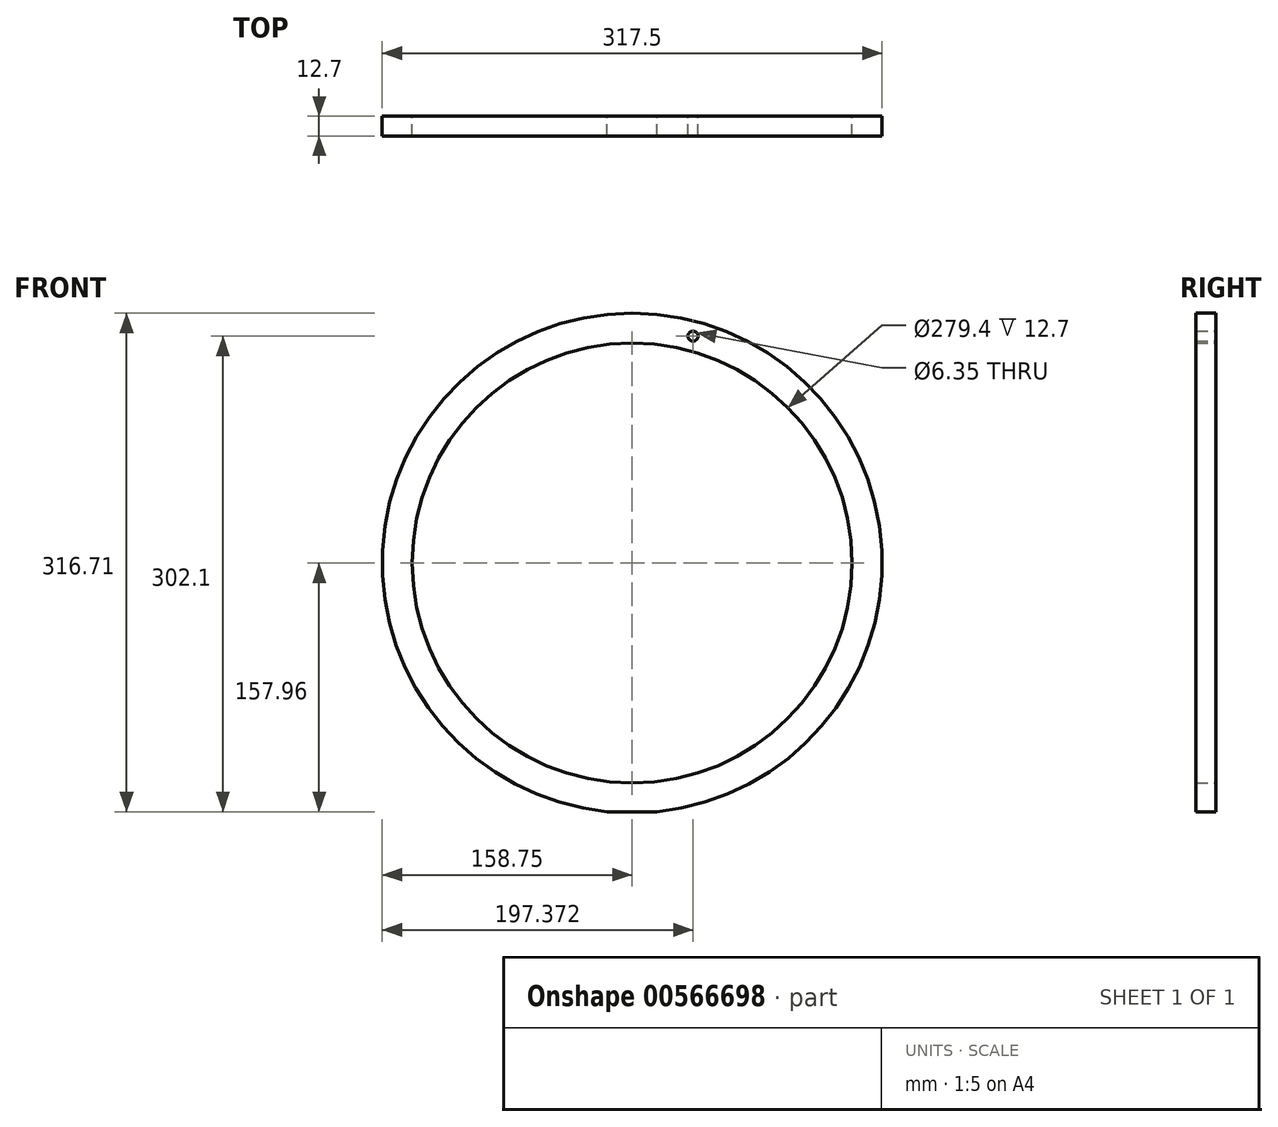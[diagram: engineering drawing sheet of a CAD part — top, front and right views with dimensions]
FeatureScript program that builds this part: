
annotation { "Feature Type Name" : "Feature", "Feature Type Description" : "" }
export const myFeature = defineFeature(function(context is Context, id is Id, definition is map)
    precondition{}
    {
        {
            var Q0;
            Q0=qCreatedBy(makeId("Front.planeOp"),FACE);
            var sketch = newSketch(context, id + "F0", { "sketchPlane" : qUnion([Q0])});
            skCircle(sketch, "E0", {"center": v(0, 0) * mm, "radius": 139.7 * mm});
            skLineSegment(sketch, "E1", {"start": v(-15.86, -157.96) * mm, "end": v(15.86, -157.96) * mm});
            skArc(sketch, "E2", {"start": v(-15.86, -157.96) * mm, "mid": v(0, -158.75) * mm, "end": v(15.86, -157.96) * mm, "construction": true});
            skArc(sketch, "E3", {"start": v(15.86, -157.96) * mm, "mid": v(0, 158.75) * mm, "end": v(-15.86, -157.96) * mm});
            skSolve(sketch);
        }
        {
            var Q0;
            Q0=makeQuery(id+"F0.imprint","IMPRINT",FACE,{"disambiguationData":[TD([[makeQuery(id+"F0.imprint","IMPRINT",EDGE,{"derivedFrom":sQuery(id+"F0.wireOp",EDGE,"E0")}),-1.0]])]});
            extrude(context, id + "F1", {"entities" : qUnion([Q0]), "depth" : 12.7 * mm, "offsetDistance" : 25.4 * mm});
        }
        {
            var Q0;
            Q0=makeQuery(id+"F0.imprint","IMPRINT",FACE,{"disambiguationData":[TD([[makeQuery(id+"F0.imprint","IMPRINT",EDGE,{"derivedFrom":sQuery(id+"F0.wireOp",EDGE,"E0")}),1.0]])]});
            var sketch = newSketch(context, id + "F2", { "sketchPlane" : qUnion([Q0])});
            skArc(sketch, "E4.0", {"start": v(15.86, -157.96) * mm, "mid": v(0, 158.75) * mm, "end": v(-15.86, -157.96) * mm, "construction": true});
            skCircle(sketch, "E5.0", {"center": v(0, 0) * mm, "radius": 139.7 * mm, "construction": true});
            skLineSegment(sketch, "E6.0", {"start": v(-15.86, -157.96) * mm, "end": v(15.86, -157.96) * mm});
            skArc(sketch, "E7.0", {"start": v(-15.86, -157.96) * mm, "mid": v(0, -158.75) * mm, "end": v(15.86, -157.96) * mm});
            skCircle(sketch, "E8", {"center": v(0, 149.22) * mm, "radius": 1.59 * mm});
            skLineSegment(sketch, "E9", {"start": v(0, 149.22) * mm, "end": v(29, 149.22) * mm, "construction": true});
            skLineSegment(sketch, "E10", {"start": v(0, 149.22) * mm, "end": v(0, 0) * mm, "construction": true});
            skCircle(sketch, "E11.1.0.0", {"center": v(2.75, 147.64) * mm, "radius": 1.59 * mm});
            skCircle(sketch, "E11.2.0.0", {"center": v(5.5, 146.05) * mm, "radius": 1.59 * mm});
            skLineSegment(sketch, "E11.direction1", {"start": v(0, 149.22) * mm, "end": v(2.75, 147.64) * mm, "construction": true});
            skCircle(sketch, "E12.cCircle", {"center": v(0, 149.22) * mm, "radius": 6.35 * mm, "construction": true});
            skLineSegment(sketch, "E12.0", {"start": v(5.5, 146.05) * mm, "end": v(0, 142.87) * mm});
            skLineSegment(sketch, "E12.1", {"start": v(0, 142.88) * mm, "end": v(-5.5, 146.05) * mm});
            skLineSegment(sketch, "E12.2", {"start": v(-5.5, 146.05) * mm, "end": v(-5.5, 152.4) * mm});
            skLineSegment(sketch, "E12.3", {"start": v(-5.5, 152.4) * mm, "end": v(0, 155.57) * mm});
            skLineSegment(sketch, "E12.4", {"start": v(0, 155.57) * mm, "end": v(5.5, 152.4) * mm});
            skLineSegment(sketch, "E12.5", {"start": v(5.5, 152.4) * mm, "end": v(5.5, 146.05) * mm});
            skLineSegment(sketch, "E13", {"start": v(0, 149.22) * mm, "end": v(-5.5, 146.05) * mm});
            skLineSegment(sketch, "E14.bottom", {"start": v(-5.5, 152.4) * mm, "end": v(5.5, 152.4) * mm});
            skLineSegment(sketch, "E14.top", {"start": v(-5.5, 146.05) * mm, "end": v(5.5, 146.05) * mm});
            skLineSegment(sketch, "E14.left", {"start": v(-5.5, 152.4) * mm, "end": v(-5.5, 146.05) * mm});
            skCircle(sketch, "E15.1.0", {"center": v(2.75, 150.81) * mm, "radius": 1.59 * mm});
            skCircle(sketch, "E15.1.1", {"center": v(5.5, 152.4) * mm, "radius": 1.59 * mm});
            skCircle(sketch, "E15.2.0", {"center": v(0, 152.4) * mm, "radius": 1.59 * mm});
            skCircle(sketch, "E15.2.1", {"center": v(0, 155.57) * mm, "radius": 1.59 * mm});
            skCircle(sketch, "E15.3.0", {"center": v(-2.75, 150.81) * mm, "radius": 1.59 * mm});
            skCircle(sketch, "E15.3.1", {"center": v(-5.5, 152.4) * mm, "radius": 1.59 * mm});
            skCircle(sketch, "E15.4.0", {"center": v(-2.75, 147.64) * mm, "radius": 1.59 * mm});
            skCircle(sketch, "E15.4.1", {"center": v(-5.5, 146.05) * mm, "radius": 1.59 * mm});
            skCircle(sketch, "E15.5.0", {"center": v(0, 146.05) * mm, "radius": 1.59 * mm});
            skCircle(sketch, "E15.5.1", {"center": v(0, 142.88) * mm, "radius": 1.59 * mm});
            skLineSegment(sketch, "E16.1.0", {"start": v(0, 149.22) * mm, "end": v(0, 142.88) * mm});
            skLineSegment(sketch, "E16.1.1", {"start": v(0, 149.22) * mm, "end": v(2.75, 150.81) * mm, "construction": true});
            skLineSegment(sketch, "E16.2.0", {"start": v(0, 149.22) * mm, "end": v(5.5, 146.05) * mm});
            skLineSegment(sketch, "E16.2.1", {"start": v(0, 149.22) * mm, "end": v(0, 152.4) * mm, "construction": true});
            skLineSegment(sketch, "E16.3.0", {"start": v(0, 149.22) * mm, "end": v(5.5, 152.4) * mm});
            skLineSegment(sketch, "E16.3.1", {"start": v(0, 149.22) * mm, "end": v(-2.75, 150.81) * mm, "construction": true});
            skLineSegment(sketch, "E16.4.0", {"start": v(0, 149.22) * mm, "end": v(0, 155.57) * mm});
            skLineSegment(sketch, "E16.4.1", {"start": v(0, 149.22) * mm, "end": v(-2.75, 147.64) * mm, "construction": true});
            skLineSegment(sketch, "E16.5.0", {"start": v(0, 149.22) * mm, "end": v(-5.5, 152.4) * mm});
            skLineSegment(sketch, "E16.5.1", {"start": v(0, 149.22) * mm, "end": v(0, 146.05) * mm, "construction": true});
            skLineSegment(sketch, "E17", {"start": v(-5.5, 152.4) * mm, "end": v(0, 142.88) * mm});
            skLineSegment(sketch, "E18", {"start": v(0, 142.87) * mm, "end": v(5.5, 152.4) * mm});
            skLineSegment(sketch, "E19", {"start": v(-2.75, 150.81) * mm, "end": v(0, 146.05) * mm});
            skLineSegment(sketch, "E20", {"start": v(0, 146.05) * mm, "end": v(2.75, 150.81) * mm});
            skLineSegment(sketch, "E21", {"start": v(2.75, 150.81) * mm, "end": v(-2.75, 150.81) * mm});
            skLineSegment(sketch, "E22", {"start": v(-2.75, 150.81) * mm, "end": v(0, 152.4) * mm});
            skLineSegment(sketch, "E23", {"start": v(0, 152.4) * mm, "end": v(2.75, 150.81) * mm});
            skLineSegment(sketch, "E24", {"start": v(2.75, 150.81) * mm, "end": v(2.75, 147.64) * mm});
            skLineSegment(sketch, "E25", {"start": v(2.75, 147.64) * mm, "end": v(0, 146.05) * mm});
            skLineSegment(sketch, "E26", {"start": v(0, 146.05) * mm, "end": v(-2.75, 147.64) * mm});
            skLineSegment(sketch, "E27", {"start": v(-2.75, 147.64) * mm, "end": v(-2.75, 150.81) * mm});
            skLineSegment(sketch, "E28", {"start": v(0, 152.4) * mm, "end": v(-2.75, 147.64) * mm});
            skLineSegment(sketch, "E29", {"start": v(0, 152.4) * mm, "end": v(2.75, 147.64) * mm});
            skLineSegment(sketch, "E30", {"start": v(2.75, 147.64) * mm, "end": v(-2.75, 147.64) * mm});
            skLineSegment(sketch, "E31", {"start": v(0, 142.88) * mm, "end": v(-2.75, 150.81) * mm});
            skLineSegment(sketch, "E32", {"start": v(0, 142.88) * mm, "end": v(2.75, 150.81) * mm});
            skLineSegment(sketch, "E33", {"start": v(5.5, 146.05) * mm, "end": v(-2.75, 147.64) * mm});
            skLineSegment(sketch, "E34", {"start": v(5.5, 146.05) * mm, "end": v(0, 152.4) * mm});
            skLineSegment(sketch, "E35", {"start": v(5.5, 152.4) * mm, "end": v(0, 146.05) * mm});
            skLineSegment(sketch, "E36", {"start": v(5.5, 152.4) * mm, "end": v(-2.75, 150.81) * mm});
            skLineSegment(sketch, "E37", {"start": v(0, 155.57) * mm, "end": v(2.75, 147.64) * mm});
            skLineSegment(sketch, "E38", {"start": v(0, 155.57) * mm, "end": v(-2.75, 147.64) * mm});
            skLineSegment(sketch, "E39", {"start": v(-5.5, 152.4) * mm, "end": v(2.75, 150.81) * mm});
            skLineSegment(sketch, "E40", {"start": v(-5.5, 152.4) * mm, "end": v(0, 146.05) * mm});
            skLineSegment(sketch, "E41", {"start": v(-5.5, 146.05) * mm, "end": v(2.75, 147.64) * mm});
            skLineSegment(sketch, "E42", {"start": v(-5.5, 146.05) * mm, "end": v(0, 152.4) * mm});
            skLineSegment(sketch, "E43", {"start": v(0, 155.57) * mm, "end": v(-5.5, 146.05) * mm});
            skLineSegment(sketch, "E44", {"start": v(0, 155.57) * mm, "end": v(5.5, 146.05) * mm});
            skCircle(sketch, "E45.1.0", {"center": v(-129.23, 74.61) * mm, "radius": 6.35 * mm, "construction": true});
            skLineSegment(sketch, "E45.1.1", {"start": v(-129.23, 80.96) * mm, "end": v(-131.98, 73.03) * mm});
            skLineSegment(sketch, "E45.1.2", {"start": v(-134.73, 71.44) * mm, "end": v(-123.73, 71.44) * mm});
            skCircle(sketch, "E45.1.3", {"center": v(-131.98, 73.03) * mm, "radius": 1.59 * mm});
            skLineSegment(sketch, "E45.1.4", {"start": v(-129.23, 74.61) * mm, "end": v(-126.48, 76.2) * mm, "construction": true});
            skLineSegment(sketch, "E45.1.5", {"start": v(-123.73, 77.79) * mm, "end": v(-129.23, 71.44) * mm});
            skLineSegment(sketch, "E45.1.6", {"start": v(-129.23, 80.96) * mm, "end": v(-126.48, 73.03) * mm});
            skCircle(sketch, "E45.1.7", {"center": v(-129.23, 77.79) * mm, "radius": 1.59 * mm});
            skCircle(sketch, "E45.1.8", {"center": v(-123.73, 77.79) * mm, "radius": 1.59 * mm});
            skLineSegment(sketch, "E45.1.9", {"start": v(-131.98, 76.2) * mm, "end": v(-126.48, 76.2) * mm});
            skLineSegment(sketch, "E45.1.10", {"start": v(-126.48, 73.03) * mm, "end": v(-129.23, 77.79) * mm});
            skCircle(sketch, "E45.1.11", {"center": v(-134.73, 71.44) * mm, "radius": 1.59 * mm});
            skLineSegment(sketch, "E45.1.12", {"start": v(-123.73, 77.79) * mm, "end": v(-131.98, 76.2) * mm});
            skLineSegment(sketch, "E45.1.13", {"start": v(-123.73, 71.44) * mm, "end": v(-129.23, 80.96) * mm});
            skCircle(sketch, "E45.1.14", {"center": v(-126.48, 76.2) * mm, "radius": 1.59 * mm});
            skLineSegment(sketch, "E45.1.15", {"start": v(-129.23, 74.61) * mm, "end": v(-134.73, 77.79) * mm});
            skCircle(sketch, "E45.1.16", {"center": v(-129.23, 68.26) * mm, "radius": 1.59 * mm});
            skLineSegment(sketch, "E45.1.17", {"start": v(-123.73, 71.44) * mm, "end": v(-129.23, 68.26) * mm});
            skCircle(sketch, "E45.1.18", {"center": v(-129.23, 74.61) * mm, "radius": 1.59 * mm});
            skCircle(sketch, "E45.1.19", {"center": v(-134.73, 77.79) * mm, "radius": 1.59 * mm});
            skCircle(sketch, "E45.1.20", {"center": v(-129.23, 71.44) * mm, "radius": 1.59 * mm});
            skLineSegment(sketch, "E45.1.21", {"start": v(-123.73, 77.79) * mm, "end": v(-123.73, 71.44) * mm});
            skLineSegment(sketch, "E45.1.22", {"start": v(-129.23, 74.61) * mm, "end": v(-126.48, 73.03) * mm, "construction": true});
            skLineSegment(sketch, "E45.1.23", {"start": v(-123.73, 71.44) * mm, "end": v(-129.23, 77.79) * mm});
            skLineSegment(sketch, "E45.1.24", {"start": v(-134.73, 77.79) * mm, "end": v(-129.23, 80.96) * mm});
            skLineSegment(sketch, "E45.1.25", {"start": v(-134.73, 71.44) * mm, "end": v(-134.73, 77.79) * mm});
            skLineSegment(sketch, "E45.1.26", {"start": v(-129.23, 68.26) * mm, "end": v(-134.73, 71.44) * mm});
            skLineSegment(sketch, "E45.1.27", {"start": v(-131.98, 76.2) * mm, "end": v(-129.23, 71.44) * mm});
            skLineSegment(sketch, "E45.1.28", {"start": v(-134.73, 77.79) * mm, "end": v(-123.73, 77.79) * mm});
            skLineSegment(sketch, "E45.1.29", {"start": v(-131.98, 73.03) * mm, "end": v(-126.48, 73.03) * mm});
            skLineSegment(sketch, "E45.1.30", {"start": v(-129.23, 68.26) * mm, "end": v(-126.48, 76.2) * mm});
            skLineSegment(sketch, "E45.1.31", {"start": v(-126.48, 76.2) * mm, "end": v(-126.48, 73.03) * mm});
            skLineSegment(sketch, "E45.1.32", {"start": v(-129.23, 74.61) * mm, "end": v(-131.98, 73.03) * mm, "construction": true});
            skLineSegment(sketch, "E45.1.33", {"start": v(-129.23, 74.61) * mm, "end": v(-134.73, 71.44) * mm});
            skCircle(sketch, "E45.1.34", {"center": v(-131.98, 76.2) * mm, "radius": 1.59 * mm});
            skLineSegment(sketch, "E45.1.35", {"start": v(-123.73, 71.44) * mm, "end": v(-131.98, 73.03) * mm});
            skCircle(sketch, "E45.1.36", {"center": v(-126.48, 73.03) * mm, "radius": 1.59 * mm});
            skLineSegment(sketch, "E45.1.37", {"start": v(-134.73, 77.79) * mm, "end": v(-126.48, 76.2) * mm});
            skLineSegment(sketch, "E45.1.38", {"start": v(-129.23, 77.79) * mm, "end": v(-131.98, 73.03) * mm});
            skLineSegment(sketch, "E45.1.39", {"start": v(-126.48, 73.03) * mm, "end": v(-129.23, 71.44) * mm});
            skLineSegment(sketch, "E45.1.40", {"start": v(-126.48, 76.2) * mm, "end": v(-129.23, 71.44) * mm});
            skCircle(sketch, "E45.1.41", {"center": v(-129.23, 80.96) * mm, "radius": 1.59 * mm});
            skLineSegment(sketch, "E45.1.42", {"start": v(-129.23, 74.61) * mm, "end": v(-129.23, 71.44) * mm, "construction": true});
            skLineSegment(sketch, "E45.1.43", {"start": v(-134.73, 77.79) * mm, "end": v(-129.23, 71.44) * mm});
            skCircle(sketch, "E45.1.44", {"center": v(-123.73, 71.44) * mm, "radius": 1.59 * mm});
            skLineSegment(sketch, "E45.1.45", {"start": v(-131.98, 73.03) * mm, "end": v(-131.98, 76.2) * mm});
            skLineSegment(sketch, "E45.1.46", {"start": v(-129.23, 74.61) * mm, "end": v(-129.23, 80.96) * mm});
            skLineSegment(sketch, "E45.1.47", {"start": v(-129.23, 68.26) * mm, "end": v(-131.98, 76.2) * mm});
            skLineSegment(sketch, "E45.1.48", {"start": v(-134.73, 71.44) * mm, "end": v(-129.23, 80.96) * mm});
            skLineSegment(sketch, "E45.1.49", {"start": v(-129.23, 74.61) * mm, "end": v(-123.73, 77.79) * mm});
            skLineSegment(sketch, "E45.1.50", {"start": v(-129.23, 74.61) * mm, "end": v(-123.73, 71.44) * mm});
            skLineSegment(sketch, "E45.1.51", {"start": v(-129.23, 80.96) * mm, "end": v(-123.73, 77.79) * mm});
            skLineSegment(sketch, "E45.1.52", {"start": v(-134.73, 71.44) * mm, "end": v(-129.23, 77.79) * mm});
            skLineSegment(sketch, "E45.1.53", {"start": v(-131.98, 76.2) * mm, "end": v(-129.23, 77.79) * mm});
            skLineSegment(sketch, "E45.1.54", {"start": v(-129.23, 71.44) * mm, "end": v(-131.98, 73.03) * mm});
            skLineSegment(sketch, "E45.1.55", {"start": v(-134.73, 77.79) * mm, "end": v(-129.23, 68.26) * mm});
            skPoint(sketch, "E45.1.56", {"position": v(-129.23, 74.61) * mm});
            skLineSegment(sketch, "E45.1.57", {"start": v(-129.23, 74.61) * mm, "end": v(-129.23, 68.26) * mm});
            skLineSegment(sketch, "E45.1.58", {"start": v(-129.23, 74.61) * mm, "end": v(-129.23, 77.79) * mm, "construction": true});
            skLineSegment(sketch, "E45.1.59", {"start": v(-129.23, 77.79) * mm, "end": v(-126.48, 76.2) * mm});
            skLineSegment(sketch, "E45.1.60", {"start": v(-134.73, 71.44) * mm, "end": v(-126.48, 73.03) * mm});
            skLineSegment(sketch, "E45.1.61", {"start": v(-129.23, 74.61) * mm, "end": v(-131.98, 76.2) * mm, "construction": true});
            skLineSegment(sketch, "E45.1.62", {"start": v(-129.23, 68.26) * mm, "end": v(-123.73, 77.79) * mm});
            skLineSegment(sketch, "E45.1.63", {"start": v(-129.23, 80.96) * mm, "end": v(-123.73, 77.79) * mm});
            skPoint(sketch, "E45.1.64", {"position": v(-129.23, 74.61) * mm});
            skLineSegment(sketch, "E45.1.65", {"start": v(-134.73, 71.44) * mm, "end": v(-129.23, 68.26) * mm});
            skCircle(sketch, "E45.2.0", {"center": v(-129.23, -74.61) * mm, "radius": 6.35 * mm, "construction": true});
            skLineSegment(sketch, "E45.2.1", {"start": v(-134.73, -71.44) * mm, "end": v(-129.23, -77.79) * mm});
            skLineSegment(sketch, "E45.2.2", {"start": v(-129.23, -80.96) * mm, "end": v(-123.73, -71.44) * mm});
            skCircle(sketch, "E45.2.3", {"center": v(-129.23, -77.79) * mm, "radius": 1.59 * mm});
            skLineSegment(sketch, "E45.2.4", {"start": v(-129.23, -74.61) * mm, "end": v(-129.23, -71.44) * mm, "construction": true});
            skLineSegment(sketch, "E45.2.5", {"start": v(-129.23, -68.26) * mm, "end": v(-126.48, -76.2) * mm});
            skLineSegment(sketch, "E45.2.6", {"start": v(-134.73, -71.44) * mm, "end": v(-126.48, -73.02) * mm});
            skCircle(sketch, "E45.2.7", {"center": v(-131.98, -73.02) * mm, "radius": 1.59 * mm});
            skCircle(sketch, "E45.2.8", {"center": v(-129.23, -68.26) * mm, "radius": 1.59 * mm});
            skLineSegment(sketch, "E45.2.9", {"start": v(-131.98, -76.2) * mm, "end": v(-129.23, -71.44) * mm});
            skLineSegment(sketch, "E45.2.10", {"start": v(-126.48, -73.02) * mm, "end": v(-131.98, -73.02) * mm});
            skCircle(sketch, "E45.2.11", {"center": v(-129.23, -80.96) * mm, "radius": 1.59 * mm});
            skLineSegment(sketch, "E45.2.12", {"start": v(-129.23, -68.26) * mm, "end": v(-131.98, -76.2) * mm});
            skLineSegment(sketch, "E45.2.13", {"start": v(-123.73, -71.44) * mm, "end": v(-134.73, -71.44) * mm});
            skCircle(sketch, "E45.2.14", {"center": v(-129.23, -71.44) * mm, "radius": 1.59 * mm});
            skLineSegment(sketch, "E45.2.15", {"start": v(-129.23, -74.61) * mm, "end": v(-134.73, -77.79) * mm});
            skCircle(sketch, "E45.2.16", {"center": v(-123.73, -77.79) * mm, "radius": 1.59 * mm});
            skLineSegment(sketch, "E45.2.17", {"start": v(-123.73, -71.44) * mm, "end": v(-123.73, -77.79) * mm});
            skCircle(sketch, "E45.2.18", {"center": v(-129.23, -74.61) * mm, "radius": 1.59 * mm});
            skCircle(sketch, "E45.2.19", {"center": v(-134.73, -77.79) * mm, "radius": 1.59 * mm});
            skCircle(sketch, "E45.2.20", {"center": v(-126.48, -76.2) * mm, "radius": 1.59 * mm});
            skLineSegment(sketch, "E45.2.21", {"start": v(-129.23, -68.26) * mm, "end": v(-123.73, -71.44) * mm});
            skLineSegment(sketch, "E45.2.22", {"start": v(-129.23, -74.61) * mm, "end": v(-126.48, -73.02) * mm, "construction": true});
            skLineSegment(sketch, "E45.2.23", {"start": v(-123.73, -71.44) * mm, "end": v(-131.98, -73.02) * mm});
            skLineSegment(sketch, "E45.2.24", {"start": v(-134.73, -77.79) * mm, "end": v(-134.73, -71.44) * mm});
            skLineSegment(sketch, "E45.2.25", {"start": v(-129.23, -80.96) * mm, "end": v(-134.73, -77.79) * mm});
            skLineSegment(sketch, "E45.2.26", {"start": v(-123.73, -77.79) * mm, "end": v(-129.23, -80.96) * mm});
            skLineSegment(sketch, "E45.2.27", {"start": v(-131.98, -76.2) * mm, "end": v(-126.48, -76.2) * mm});
            skLineSegment(sketch, "E45.2.28", {"start": v(-134.73, -77.79) * mm, "end": v(-129.23, -68.26) * mm});
            skLineSegment(sketch, "E45.2.29", {"start": v(-129.23, -77.79) * mm, "end": v(-126.48, -73.02) * mm});
            skLineSegment(sketch, "E45.2.30", {"start": v(-123.73, -77.79) * mm, "end": v(-129.23, -71.44) * mm});
            skLineSegment(sketch, "E45.2.31", {"start": v(-129.23, -71.44) * mm, "end": v(-126.48, -73.02) * mm});
            skLineSegment(sketch, "E45.2.32", {"start": v(-129.23, -74.61) * mm, "end": v(-129.23, -77.79) * mm, "construction": true});
            skLineSegment(sketch, "E45.2.33", {"start": v(-129.23, -74.61) * mm, "end": v(-129.23, -80.96) * mm});
            skCircle(sketch, "E45.2.34", {"center": v(-131.98, -76.2) * mm, "radius": 1.59 * mm});
            skLineSegment(sketch, "E45.2.35", {"start": v(-123.73, -71.44) * mm, "end": v(-129.23, -77.79) * mm});
            skCircle(sketch, "E45.2.36", {"center": v(-126.48, -73.02) * mm, "radius": 1.59 * mm});
            skLineSegment(sketch, "E45.2.37", {"start": v(-134.73, -77.79) * mm, "end": v(-129.23, -71.44) * mm});
            skLineSegment(sketch, "E45.2.38", {"start": v(-131.98, -73.02) * mm, "end": v(-129.23, -77.79) * mm});
            skLineSegment(sketch, "E45.2.39", {"start": v(-126.48, -73.02) * mm, "end": v(-126.48, -76.2) * mm});
            skLineSegment(sketch, "E45.2.40", {"start": v(-129.23, -71.44) * mm, "end": v(-126.48, -76.2) * mm});
            skCircle(sketch, "E45.2.41", {"center": v(-134.73, -71.44) * mm, "radius": 1.59 * mm});
            skLineSegment(sketch, "E45.2.42", {"start": v(-129.23, -74.61) * mm, "end": v(-126.48, -76.2) * mm, "construction": true});
            skLineSegment(sketch, "E45.2.43", {"start": v(-134.73, -77.79) * mm, "end": v(-126.48, -76.2) * mm});
            skCircle(sketch, "E45.2.44", {"center": v(-123.73, -71.44) * mm, "radius": 1.59 * mm});
            skLineSegment(sketch, "E45.2.45", {"start": v(-129.23, -77.79) * mm, "end": v(-131.98, -76.2) * mm});
            skLineSegment(sketch, "E45.2.46", {"start": v(-129.23, -74.61) * mm, "end": v(-134.73, -71.44) * mm});
            skLineSegment(sketch, "E45.2.47", {"start": v(-123.73, -77.79) * mm, "end": v(-131.98, -76.2) * mm});
            skLineSegment(sketch, "E45.2.48", {"start": v(-129.23, -80.96) * mm, "end": v(-134.73, -71.44) * mm});
            skLineSegment(sketch, "E45.2.49", {"start": v(-129.23, -74.61) * mm, "end": v(-129.23, -68.26) * mm});
            skLineSegment(sketch, "E45.2.50", {"start": v(-129.23, -74.61) * mm, "end": v(-123.73, -71.44) * mm});
            skLineSegment(sketch, "E45.2.51", {"start": v(-134.73, -71.44) * mm, "end": v(-129.23, -68.26) * mm});
            skLineSegment(sketch, "E45.2.52", {"start": v(-129.23, -80.96) * mm, "end": v(-131.98, -73.02) * mm});
            skLineSegment(sketch, "E45.2.53", {"start": v(-131.98, -76.2) * mm, "end": v(-131.98, -73.02) * mm});
            skLineSegment(sketch, "E45.2.54", {"start": v(-126.48, -76.2) * mm, "end": v(-129.23, -77.79) * mm});
            skLineSegment(sketch, "E45.2.55", {"start": v(-134.73, -77.79) * mm, "end": v(-123.73, -77.79) * mm});
            skPoint(sketch, "E45.2.56", {"position": v(-129.23, -74.61) * mm});
            skLineSegment(sketch, "E45.2.57", {"start": v(-129.23, -74.61) * mm, "end": v(-123.73, -77.79) * mm});
            skLineSegment(sketch, "E45.2.58", {"start": v(-129.23, -74.61) * mm, "end": v(-131.98, -73.02) * mm, "construction": true});
            skLineSegment(sketch, "E45.2.59", {"start": v(-131.98, -73.02) * mm, "end": v(-129.23, -71.44) * mm});
            skLineSegment(sketch, "E45.2.60", {"start": v(-129.23, -80.96) * mm, "end": v(-126.48, -73.02) * mm});
            skLineSegment(sketch, "E45.2.61", {"start": v(-129.23, -74.61) * mm, "end": v(-131.98, -76.2) * mm, "construction": true});
            skLineSegment(sketch, "E45.2.62", {"start": v(-123.73, -77.79) * mm, "end": v(-129.23, -68.26) * mm});
            skLineSegment(sketch, "E45.2.63", {"start": v(-134.73, -71.44) * mm, "end": v(-129.23, -68.26) * mm});
            skPoint(sketch, "E45.2.64", {"position": v(-129.23, -74.61) * mm});
            skLineSegment(sketch, "E45.2.65", {"start": v(-129.23, -80.96) * mm, "end": v(-123.73, -77.79) * mm});
            skCircle(sketch, "E45.3.0", {"center": v(0, -149.22) * mm, "radius": 6.35 * mm, "construction": true});
            skLineSegment(sketch, "E45.3.1", {"start": v(-5.5, -152.4) * mm, "end": v(2.75, -150.81) * mm});
            skLineSegment(sketch, "E45.3.2", {"start": v(5.5, -152.4) * mm, "end": v(0, -142.88) * mm});
            skCircle(sketch, "E45.3.3", {"center": v(2.75, -150.81) * mm, "radius": 1.59 * mm});
            skLineSegment(sketch, "E45.3.4", {"start": v(0, -149.22) * mm, "end": v(-2.75, -147.64) * mm, "construction": true});
            skLineSegment(sketch, "E45.3.5", {"start": v(-5.5, -146.05) * mm, "end": v(2.75, -147.64) * mm});
            skLineSegment(sketch, "E45.3.6", {"start": v(-5.5, -152.4) * mm, "end": v(0, -146.05) * mm});
            skCircle(sketch, "E45.3.7", {"center": v(-2.75, -150.81) * mm, "radius": 1.59 * mm});
            skCircle(sketch, "E45.3.8", {"center": v(-5.5, -146.05) * mm, "radius": 1.59 * mm});
            skLineSegment(sketch, "E45.3.9", {"start": v(0, -152.4) * mm, "end": v(-2.75, -147.64) * mm});
            skLineSegment(sketch, "E45.3.10", {"start": v(0, -146.05) * mm, "end": v(-2.75, -150.81) * mm});
            skCircle(sketch, "E45.3.11", {"center": v(5.5, -152.4) * mm, "radius": 1.59 * mm});
            skLineSegment(sketch, "E45.3.12", {"start": v(-5.5, -146.05) * mm, "end": v(0, -152.4) * mm});
            skLineSegment(sketch, "E45.3.13", {"start": v(0, -142.87) * mm, "end": v(-5.5, -152.4) * mm});
            skCircle(sketch, "E45.3.14", {"center": v(-2.75, -147.64) * mm, "radius": 1.59 * mm});
            skLineSegment(sketch, "E45.3.15", {"start": v(0, -149.22) * mm, "end": v(0, -155.57) * mm});
            skCircle(sketch, "E45.3.16", {"center": v(5.5, -146.05) * mm, "radius": 1.59 * mm});
            skLineSegment(sketch, "E45.3.17", {"start": v(0, -142.88) * mm, "end": v(5.5, -146.05) * mm});
            skCircle(sketch, "E45.3.18", {"center": v(0, -149.22) * mm, "radius": 1.59 * mm});
            skCircle(sketch, "E45.3.19", {"center": v(0, -155.57) * mm, "radius": 1.59 * mm});
            skCircle(sketch, "E45.3.20", {"center": v(2.75, -147.64) * mm, "radius": 1.59 * mm});
            skLineSegment(sketch, "E45.3.21", {"start": v(-5.5, -146.05) * mm, "end": v(0, -142.87) * mm});
            skLineSegment(sketch, "E45.3.22", {"start": v(0, -149.22) * mm, "end": v(0, -146.05) * mm, "construction": true});
            skLineSegment(sketch, "E45.3.23", {"start": v(0, -142.88) * mm, "end": v(-2.75, -150.81) * mm});
            skLineSegment(sketch, "E45.3.24", {"start": v(0, -155.57) * mm, "end": v(-5.5, -152.4) * mm});
            skLineSegment(sketch, "E45.3.25", {"start": v(5.5, -152.4) * mm, "end": v(0, -155.57) * mm});
            skLineSegment(sketch, "E45.3.26", {"start": v(5.5, -146.05) * mm, "end": v(5.5, -152.4) * mm});
            skLineSegment(sketch, "E45.3.27", {"start": v(0, -152.4) * mm, "end": v(2.75, -147.64) * mm});
            skLineSegment(sketch, "E45.3.28", {"start": v(0, -155.57) * mm, "end": v(-5.5, -146.05) * mm});
            skLineSegment(sketch, "E45.3.29", {"start": v(2.75, -150.81) * mm, "end": v(0, -146.05) * mm});
            skLineSegment(sketch, "E45.3.30", {"start": v(5.5, -146.05) * mm, "end": v(-2.75, -147.64) * mm});
            skLineSegment(sketch, "E45.3.31", {"start": v(-2.75, -147.64) * mm, "end": v(0, -146.05) * mm});
            skLineSegment(sketch, "E45.3.32", {"start": v(0, -149.22) * mm, "end": v(2.75, -150.81) * mm, "construction": true});
            skLineSegment(sketch, "E45.3.33", {"start": v(0, -149.22) * mm, "end": v(5.5, -152.4) * mm});
            skCircle(sketch, "E45.3.34", {"center": v(0, -152.4) * mm, "radius": 1.59 * mm});
            skLineSegment(sketch, "E45.3.35", {"start": v(0, -142.88) * mm, "end": v(2.75, -150.81) * mm});
            skCircle(sketch, "E45.3.36", {"center": v(0, -146.05) * mm, "radius": 1.59 * mm});
            skLineSegment(sketch, "E45.3.37", {"start": v(0, -155.57) * mm, "end": v(-2.75, -147.64) * mm});
            skLineSegment(sketch, "E45.3.38", {"start": v(-2.75, -150.81) * mm, "end": v(2.75, -150.81) * mm});
            skLineSegment(sketch, "E45.3.39", {"start": v(0, -146.05) * mm, "end": v(2.75, -147.64) * mm});
            skLineSegment(sketch, "E45.3.40", {"start": v(-2.75, -147.64) * mm, "end": v(2.75, -147.64) * mm});
            skCircle(sketch, "E45.3.41", {"center": v(-5.5, -152.4) * mm, "radius": 1.59 * mm});
            skLineSegment(sketch, "E45.3.42", {"start": v(0, -149.22) * mm, "end": v(2.75, -147.64) * mm, "construction": true});
            skLineSegment(sketch, "E45.3.43", {"start": v(0, -155.57) * mm, "end": v(2.75, -147.64) * mm});
            skCircle(sketch, "E45.3.44", {"center": v(0, -142.88) * mm, "radius": 1.59 * mm});
            skLineSegment(sketch, "E45.3.45", {"start": v(2.75, -150.81) * mm, "end": v(0, -152.4) * mm});
            skLineSegment(sketch, "E45.3.46", {"start": v(0, -149.22) * mm, "end": v(-5.5, -152.4) * mm});
            skLineSegment(sketch, "E45.3.47", {"start": v(5.5, -146.05) * mm, "end": v(0, -152.4) * mm});
            skLineSegment(sketch, "E45.3.48", {"start": v(5.5, -152.4) * mm, "end": v(-5.5, -152.4) * mm});
            skLineSegment(sketch, "E45.3.49", {"start": v(0, -149.22) * mm, "end": v(-5.5, -146.05) * mm});
            skLineSegment(sketch, "E45.3.50", {"start": v(0, -149.22) * mm, "end": v(0, -142.88) * mm});
            skLineSegment(sketch, "E45.3.51", {"start": v(-5.5, -152.4) * mm, "end": v(-5.5, -146.05) * mm});
            skLineSegment(sketch, "E45.3.52", {"start": v(5.5, -152.4) * mm, "end": v(-2.75, -150.81) * mm});
            skLineSegment(sketch, "E45.3.53", {"start": v(0, -152.4) * mm, "end": v(-2.75, -150.81) * mm});
            skLineSegment(sketch, "E45.3.54", {"start": v(2.75, -147.64) * mm, "end": v(2.75, -150.81) * mm});
            skLineSegment(sketch, "E45.3.55", {"start": v(0, -155.57) * mm, "end": v(5.5, -146.05) * mm});
            skPoint(sketch, "E45.3.56", {"position": v(0, -149.22) * mm});
            skLineSegment(sketch, "E45.3.57", {"start": v(0, -149.22) * mm, "end": v(5.5, -146.05) * mm});
            skLineSegment(sketch, "E45.3.58", {"start": v(0, -149.22) * mm, "end": v(-2.75, -150.81) * mm, "construction": true});
            skLineSegment(sketch, "E45.3.59", {"start": v(-2.75, -150.81) * mm, "end": v(-2.75, -147.64) * mm});
            skLineSegment(sketch, "E45.3.60", {"start": v(5.5, -152.4) * mm, "end": v(0, -146.05) * mm});
            skLineSegment(sketch, "E45.3.61", {"start": v(0, -149.22) * mm, "end": v(0, -152.4) * mm, "construction": true});
            skLineSegment(sketch, "E45.3.62", {"start": v(5.5, -146.05) * mm, "end": v(-5.5, -146.05) * mm});
            skLineSegment(sketch, "E45.3.63", {"start": v(-5.5, -152.4) * mm, "end": v(-5.5, -146.05) * mm});
            skPoint(sketch, "E45.3.64", {"position": v(0, -149.22) * mm});
            skLineSegment(sketch, "E45.3.65", {"start": v(5.5, -152.4) * mm, "end": v(5.5, -146.05) * mm});
            skCircle(sketch, "E45.4.0", {"center": v(129.23, -74.61) * mm, "radius": 6.35 * mm, "construction": true});
            skLineSegment(sketch, "E45.4.1", {"start": v(129.23, -80.96) * mm, "end": v(131.98, -73.03) * mm});
            skLineSegment(sketch, "E45.4.2", {"start": v(134.73, -71.44) * mm, "end": v(123.73, -71.44) * mm});
            skCircle(sketch, "E45.4.3", {"center": v(131.98, -73.03) * mm, "radius": 1.59 * mm});
            skLineSegment(sketch, "E45.4.4", {"start": v(129.23, -74.61) * mm, "end": v(126.48, -76.2) * mm, "construction": true});
            skLineSegment(sketch, "E45.4.5", {"start": v(123.73, -77.79) * mm, "end": v(129.23, -71.44) * mm});
            skLineSegment(sketch, "E45.4.6", {"start": v(129.23, -80.96) * mm, "end": v(126.48, -73.03) * mm});
            skCircle(sketch, "E45.4.7", {"center": v(129.23, -77.79) * mm, "radius": 1.59 * mm});
            skCircle(sketch, "E45.4.8", {"center": v(123.73, -77.79) * mm, "radius": 1.59 * mm});
            skLineSegment(sketch, "E45.4.9", {"start": v(131.98, -76.2) * mm, "end": v(126.48, -76.2) * mm});
            skLineSegment(sketch, "E45.4.10", {"start": v(126.48, -73.03) * mm, "end": v(129.23, -77.79) * mm});
            skCircle(sketch, "E45.4.11", {"center": v(134.73, -71.44) * mm, "radius": 1.59 * mm});
            skLineSegment(sketch, "E45.4.12", {"start": v(123.73, -77.79) * mm, "end": v(131.98, -76.2) * mm});
            skLineSegment(sketch, "E45.4.13", {"start": v(123.73, -71.44) * mm, "end": v(129.23, -80.96) * mm});
            skCircle(sketch, "E45.4.14", {"center": v(126.48, -76.2) * mm, "radius": 1.59 * mm});
            skLineSegment(sketch, "E45.4.15", {"start": v(129.23, -74.61) * mm, "end": v(134.73, -77.79) * mm});
            skCircle(sketch, "E45.4.16", {"center": v(129.23, -68.26) * mm, "radius": 1.59 * mm});
            skLineSegment(sketch, "E45.4.17", {"start": v(123.73, -71.44) * mm, "end": v(129.23, -68.26) * mm});
            skCircle(sketch, "E45.4.18", {"center": v(129.23, -74.61) * mm, "radius": 1.59 * mm});
            skCircle(sketch, "E45.4.19", {"center": v(134.73, -77.79) * mm, "radius": 1.59 * mm});
            skCircle(sketch, "E45.4.20", {"center": v(129.23, -71.44) * mm, "radius": 1.59 * mm});
            skLineSegment(sketch, "E45.4.21", {"start": v(123.73, -77.79) * mm, "end": v(123.73, -71.44) * mm});
            skLineSegment(sketch, "E45.4.22", {"start": v(129.23, -74.61) * mm, "end": v(126.48, -73.03) * mm, "construction": true});
            skLineSegment(sketch, "E45.4.23", {"start": v(123.73, -71.44) * mm, "end": v(129.23, -77.79) * mm});
            skLineSegment(sketch, "E45.4.24", {"start": v(134.73, -77.79) * mm, "end": v(129.23, -80.96) * mm});
            skLineSegment(sketch, "E45.4.25", {"start": v(134.73, -71.44) * mm, "end": v(134.73, -77.79) * mm});
            skLineSegment(sketch, "E45.4.26", {"start": v(129.23, -68.26) * mm, "end": v(134.73, -71.44) * mm});
            skLineSegment(sketch, "E45.4.27", {"start": v(131.98, -76.2) * mm, "end": v(129.23, -71.44) * mm});
            skLineSegment(sketch, "E45.4.28", {"start": v(134.73, -77.79) * mm, "end": v(123.73, -77.79) * mm});
            skLineSegment(sketch, "E45.4.29", {"start": v(131.98, -73.03) * mm, "end": v(126.48, -73.03) * mm});
            skLineSegment(sketch, "E45.4.30", {"start": v(129.23, -68.26) * mm, "end": v(126.48, -76.2) * mm});
            skLineSegment(sketch, "E45.4.31", {"start": v(126.48, -76.2) * mm, "end": v(126.48, -73.03) * mm});
            skLineSegment(sketch, "E45.4.32", {"start": v(129.23, -74.61) * mm, "end": v(131.98, -73.03) * mm, "construction": true});
            skLineSegment(sketch, "E45.4.33", {"start": v(129.23, -74.61) * mm, "end": v(134.73, -71.44) * mm});
            skCircle(sketch, "E45.4.34", {"center": v(131.98, -76.2) * mm, "radius": 1.59 * mm});
            skLineSegment(sketch, "E45.4.35", {"start": v(123.73, -71.44) * mm, "end": v(131.98, -73.03) * mm});
            skCircle(sketch, "E45.4.36", {"center": v(126.48, -73.03) * mm, "radius": 1.59 * mm});
            skLineSegment(sketch, "E45.4.37", {"start": v(134.73, -77.79) * mm, "end": v(126.48, -76.2) * mm});
            skLineSegment(sketch, "E45.4.38", {"start": v(129.23, -77.79) * mm, "end": v(131.98, -73.03) * mm});
            skLineSegment(sketch, "E45.4.39", {"start": v(126.48, -73.03) * mm, "end": v(129.23, -71.44) * mm});
            skLineSegment(sketch, "E45.4.40", {"start": v(126.48, -76.2) * mm, "end": v(129.23, -71.44) * mm});
            skCircle(sketch, "E45.4.41", {"center": v(129.23, -80.96) * mm, "radius": 1.59 * mm});
            skLineSegment(sketch, "E45.4.42", {"start": v(129.23, -74.61) * mm, "end": v(129.23, -71.44) * mm, "construction": true});
            skLineSegment(sketch, "E45.4.43", {"start": v(134.73, -77.79) * mm, "end": v(129.23, -71.44) * mm});
            skCircle(sketch, "E45.4.44", {"center": v(123.73, -71.44) * mm, "radius": 1.59 * mm});
            skLineSegment(sketch, "E45.4.45", {"start": v(131.98, -73.03) * mm, "end": v(131.98, -76.2) * mm});
            skLineSegment(sketch, "E45.4.46", {"start": v(129.23, -74.61) * mm, "end": v(129.23, -80.96) * mm});
            skLineSegment(sketch, "E45.4.47", {"start": v(129.23, -68.26) * mm, "end": v(131.98, -76.2) * mm});
            skLineSegment(sketch, "E45.4.48", {"start": v(134.73, -71.44) * mm, "end": v(129.23, -80.96) * mm});
            skLineSegment(sketch, "E45.4.49", {"start": v(129.23, -74.61) * mm, "end": v(123.73, -77.79) * mm});
            skLineSegment(sketch, "E45.4.50", {"start": v(129.23, -74.61) * mm, "end": v(123.73, -71.44) * mm});
            skLineSegment(sketch, "E45.4.51", {"start": v(129.23, -80.96) * mm, "end": v(123.73, -77.79) * mm});
            skLineSegment(sketch, "E45.4.52", {"start": v(134.73, -71.44) * mm, "end": v(129.23, -77.79) * mm});
            skLineSegment(sketch, "E45.4.53", {"start": v(131.98, -76.2) * mm, "end": v(129.23, -77.79) * mm});
            skLineSegment(sketch, "E45.4.54", {"start": v(129.23, -71.44) * mm, "end": v(131.98, -73.03) * mm});
            skLineSegment(sketch, "E45.4.55", {"start": v(134.73, -77.79) * mm, "end": v(129.23, -68.26) * mm});
            skPoint(sketch, "E45.4.56", {"position": v(129.23, -74.61) * mm});
            skLineSegment(sketch, "E45.4.57", {"start": v(129.23, -74.61) * mm, "end": v(129.23, -68.26) * mm});
            skLineSegment(sketch, "E45.4.58", {"start": v(129.23, -74.61) * mm, "end": v(129.23, -77.79) * mm, "construction": true});
            skLineSegment(sketch, "E45.4.59", {"start": v(129.23, -77.79) * mm, "end": v(126.48, -76.2) * mm});
            skLineSegment(sketch, "E45.4.60", {"start": v(134.73, -71.44) * mm, "end": v(126.48, -73.03) * mm});
            skLineSegment(sketch, "E45.4.61", {"start": v(129.23, -74.61) * mm, "end": v(131.98, -76.2) * mm, "construction": true});
            skLineSegment(sketch, "E45.4.62", {"start": v(129.23, -68.26) * mm, "end": v(123.73, -77.79) * mm});
            skLineSegment(sketch, "E45.4.63", {"start": v(129.23, -80.96) * mm, "end": v(123.73, -77.79) * mm});
            skPoint(sketch, "E45.4.64", {"position": v(129.23, -74.61) * mm});
            skLineSegment(sketch, "E45.4.65", {"start": v(134.73, -71.44) * mm, "end": v(129.23, -68.26) * mm});
            skCircle(sketch, "E45.5.0", {"center": v(129.23, 74.61) * mm, "radius": 6.35 * mm, "construction": true});
            skLineSegment(sketch, "E45.5.1", {"start": v(134.73, 71.44) * mm, "end": v(129.23, 77.79) * mm});
            skLineSegment(sketch, "E45.5.2", {"start": v(129.23, 80.96) * mm, "end": v(123.73, 71.44) * mm});
            skCircle(sketch, "E45.5.3", {"center": v(129.23, 77.79) * mm, "radius": 1.59 * mm});
            skLineSegment(sketch, "E45.5.4", {"start": v(129.23, 74.61) * mm, "end": v(129.23, 71.44) * mm, "construction": true});
            skLineSegment(sketch, "E45.5.5", {"start": v(129.23, 68.26) * mm, "end": v(126.48, 76.2) * mm});
            skLineSegment(sketch, "E45.5.6", {"start": v(134.73, 71.44) * mm, "end": v(126.48, 73.03) * mm});
            skCircle(sketch, "E45.5.7", {"center": v(131.98, 73.02) * mm, "radius": 1.59 * mm});
            skCircle(sketch, "E45.5.8", {"center": v(129.23, 68.26) * mm, "radius": 1.59 * mm});
            skLineSegment(sketch, "E45.5.9", {"start": v(131.98, 76.2) * mm, "end": v(129.23, 71.44) * mm});
            skLineSegment(sketch, "E45.5.10", {"start": v(126.48, 73.03) * mm, "end": v(131.98, 73.03) * mm});
            skCircle(sketch, "E45.5.11", {"center": v(129.23, 80.96) * mm, "radius": 1.59 * mm});
            skLineSegment(sketch, "E45.5.12", {"start": v(129.23, 68.26) * mm, "end": v(131.98, 76.2) * mm});
            skLineSegment(sketch, "E45.5.13", {"start": v(123.73, 71.44) * mm, "end": v(134.73, 71.44) * mm});
            skCircle(sketch, "E45.5.14", {"center": v(129.23, 71.44) * mm, "radius": 1.59 * mm});
            skLineSegment(sketch, "E45.5.15", {"start": v(129.23, 74.61) * mm, "end": v(134.73, 77.79) * mm});
            skCircle(sketch, "E45.5.16", {"center": v(123.73, 77.79) * mm, "radius": 1.59 * mm});
            skLineSegment(sketch, "E45.5.17", {"start": v(123.73, 71.44) * mm, "end": v(123.73, 77.79) * mm});
            skCircle(sketch, "E45.5.18", {"center": v(129.23, 74.61) * mm, "radius": 1.59 * mm});
            skCircle(sketch, "E45.5.19", {"center": v(134.73, 77.79) * mm, "radius": 1.59 * mm});
            skCircle(sketch, "E45.5.20", {"center": v(126.48, 76.2) * mm, "radius": 1.59 * mm});
            skLineSegment(sketch, "E45.5.21", {"start": v(129.23, 68.26) * mm, "end": v(123.73, 71.44) * mm});
            skLineSegment(sketch, "E45.5.22", {"start": v(129.23, 74.61) * mm, "end": v(126.48, 73.03) * mm, "construction": true});
            skLineSegment(sketch, "E45.5.23", {"start": v(123.73, 71.44) * mm, "end": v(131.98, 73.02) * mm});
            skLineSegment(sketch, "E45.5.24", {"start": v(134.73, 77.79) * mm, "end": v(134.73, 71.44) * mm});
            skLineSegment(sketch, "E45.5.25", {"start": v(129.23, 80.96) * mm, "end": v(134.73, 77.79) * mm});
            skLineSegment(sketch, "E45.5.26", {"start": v(123.73, 77.79) * mm, "end": v(129.23, 80.96) * mm});
            skLineSegment(sketch, "E45.5.27", {"start": v(131.98, 76.2) * mm, "end": v(126.48, 76.2) * mm});
            skLineSegment(sketch, "E45.5.28", {"start": v(134.73, 77.79) * mm, "end": v(129.23, 68.26) * mm});
            skLineSegment(sketch, "E45.5.29", {"start": v(129.23, 77.79) * mm, "end": v(126.48, 73.03) * mm});
            skLineSegment(sketch, "E45.5.30", {"start": v(123.73, 77.79) * mm, "end": v(129.23, 71.44) * mm});
            skLineSegment(sketch, "E45.5.31", {"start": v(129.23, 71.44) * mm, "end": v(126.48, 73.03) * mm});
            skLineSegment(sketch, "E45.5.32", {"start": v(129.23, 74.61) * mm, "end": v(129.23, 77.79) * mm, "construction": true});
            skLineSegment(sketch, "E45.5.33", {"start": v(129.23, 74.61) * mm, "end": v(129.23, 80.96) * mm});
            skCircle(sketch, "E45.5.34", {"center": v(131.98, 76.2) * mm, "radius": 1.59 * mm});
            skLineSegment(sketch, "E45.5.35", {"start": v(123.73, 71.44) * mm, "end": v(129.23, 77.79) * mm});
            skCircle(sketch, "E45.5.36", {"center": v(126.48, 73.02) * mm, "radius": 1.59 * mm});
            skLineSegment(sketch, "E45.5.37", {"start": v(134.73, 77.79) * mm, "end": v(129.23, 71.44) * mm});
            skLineSegment(sketch, "E45.5.38", {"start": v(131.98, 73.03) * mm, "end": v(129.23, 77.79) * mm});
            skLineSegment(sketch, "E45.5.39", {"start": v(126.48, 73.03) * mm, "end": v(126.48, 76.2) * mm});
            skLineSegment(sketch, "E45.5.40", {"start": v(129.23, 71.44) * mm, "end": v(126.48, 76.2) * mm});
            skCircle(sketch, "E45.5.41", {"center": v(134.73, 71.44) * mm, "radius": 1.59 * mm});
            skLineSegment(sketch, "E45.5.42", {"start": v(129.23, 74.61) * mm, "end": v(126.48, 76.2) * mm, "construction": true});
            skLineSegment(sketch, "E45.5.43", {"start": v(134.73, 77.79) * mm, "end": v(126.48, 76.2) * mm});
            skCircle(sketch, "E45.5.44", {"center": v(123.73, 71.44) * mm, "radius": 1.59 * mm});
            skLineSegment(sketch, "E45.5.45", {"start": v(129.23, 77.79) * mm, "end": v(131.98, 76.2) * mm});
            skLineSegment(sketch, "E45.5.46", {"start": v(129.23, 74.61) * mm, "end": v(134.73, 71.44) * mm});
            skLineSegment(sketch, "E45.5.47", {"start": v(123.73, 77.79) * mm, "end": v(131.98, 76.2) * mm});
            skLineSegment(sketch, "E45.5.48", {"start": v(129.23, 80.96) * mm, "end": v(134.73, 71.44) * mm});
            skLineSegment(sketch, "E45.5.49", {"start": v(129.23, 74.61) * mm, "end": v(129.23, 68.26) * mm});
            skLineSegment(sketch, "E45.5.50", {"start": v(129.23, 74.61) * mm, "end": v(123.73, 71.44) * mm});
            skLineSegment(sketch, "E45.5.51", {"start": v(134.73, 71.44) * mm, "end": v(129.23, 68.26) * mm});
            skLineSegment(sketch, "E45.5.52", {"start": v(129.23, 80.96) * mm, "end": v(131.98, 73.03) * mm});
            skLineSegment(sketch, "E45.5.53", {"start": v(131.98, 76.2) * mm, "end": v(131.98, 73.03) * mm});
            skLineSegment(sketch, "E45.5.54", {"start": v(126.48, 76.2) * mm, "end": v(129.23, 77.79) * mm});
            skLineSegment(sketch, "E45.5.55", {"start": v(134.73, 77.79) * mm, "end": v(123.73, 77.79) * mm});
            skPoint(sketch, "E45.5.56", {"position": v(129.23, 74.61) * mm});
            skLineSegment(sketch, "E45.5.57", {"start": v(129.23, 74.61) * mm, "end": v(123.73, 77.79) * mm});
            skLineSegment(sketch, "E45.5.58", {"start": v(129.23, 74.61) * mm, "end": v(131.98, 73.03) * mm, "construction": true});
            skLineSegment(sketch, "E45.5.59", {"start": v(131.98, 73.03) * mm, "end": v(129.23, 71.44) * mm});
            skLineSegment(sketch, "E45.5.60", {"start": v(129.23, 80.96) * mm, "end": v(126.48, 73.03) * mm});
            skLineSegment(sketch, "E45.5.61", {"start": v(129.23, 74.61) * mm, "end": v(131.98, 76.2) * mm, "construction": true});
            skLineSegment(sketch, "E45.5.62", {"start": v(123.73, 77.79) * mm, "end": v(129.23, 68.26) * mm});
            skLineSegment(sketch, "E45.5.63", {"start": v(134.73, 71.44) * mm, "end": v(129.23, 68.26) * mm});
            skPoint(sketch, "E45.5.64", {"position": v(129.23, 74.61) * mm});
            skLineSegment(sketch, "E45.5.65", {"start": v(129.23, 80.96) * mm, "end": v(123.73, 77.79) * mm});
            skSolve(sketch);
        }
        {
            var Q0;
            Q0=qCreatedBy(makeId("Front.planeOp"),FACE);
            var sketch = newSketch(context, id + "F3", { "sketchPlane" : qUnion([Q0])});
            skLineSegment(sketch, "E46", {"start": v(0, 0) * mm, "end": v(74.61, 129.23) * mm, "construction": true});
            skCircle(sketch, "E47.cCircle", {"center": v(74.61, 129.23) * mm, "radius": 2.54 * mm, "construction": true});
            skLineSegment(sketch, "E47.0", {"start": v(73.34, 127.03) * mm, "end": v(72.07, 129.23) * mm, "construction": true});
            skLineSegment(sketch, "E47.1", {"start": v(72.07, 129.23) * mm, "end": v(73.34, 131.43) * mm, "construction": true});
            skLineSegment(sketch, "E47.2", {"start": v(73.34, 131.43) * mm, "end": v(75.88, 131.43) * mm, "construction": true});
            skLineSegment(sketch, "E47.3", {"start": v(75.88, 131.43) * mm, "end": v(77.15, 129.23) * mm, "construction": true});
            skLineSegment(sketch, "E47.4", {"start": v(77.15, 129.23) * mm, "end": v(75.88, 127.03) * mm, "construction": true});
            skLineSegment(sketch, "E47.5", {"start": v(75.88, 127.03) * mm, "end": v(73.34, 127.03) * mm, "construction": true});
            skCircle(sketch, "E48", {"center": v(75.88, 131.43) * mm, "radius": 2.54 * mm});
            skCircle(sketch, "E49", {"center": v(77.15, 129.23) * mm, "radius": 2.54 * mm});
            skCircle(sketch, "E50", {"center": v(75.88, 127.03) * mm, "radius": 2.54 * mm});
            skCircle(sketch, "E51", {"center": v(73.34, 127.03) * mm, "radius": 2.54 * mm});
            skCircle(sketch, "E52", {"center": v(72.07, 129.23) * mm, "radius": 2.54 * mm});
            skCircle(sketch, "E53", {"center": v(73.34, 131.43) * mm, "radius": 2.54 * mm});
            skCircle(sketch, "E54", {"center": v(74.61, 133.63) * mm, "radius": 2.54 * mm});
            skCircle(sketch, "E55", {"center": v(70.8, 131.43) * mm, "radius": 2.54 * mm});
            skCircle(sketch, "E56", {"center": v(70.8, 127.03) * mm, "radius": 2.54 * mm});
            skCircle(sketch, "E57", {"center": v(78.42, 127.03) * mm, "radius": 2.54 * mm});
            skCircle(sketch, "E58", {"center": v(78.42, 131.43) * mm, "radius": 2.54 * mm});
            skCircle(sketch, "E59", {"center": v(77.15, 133.63) * mm, "radius": 2.54 * mm});
            skCircle(sketch, "E60", {"center": v(77.15, 124.83) * mm, "radius": 2.54 * mm});
            skCircle(sketch, "E61", {"center": v(72.07, 124.83) * mm, "radius": 2.54 * mm});
            skCircle(sketch, "E62", {"center": v(74.61, 124.83) * mm, "radius": 2.54 * mm});
            skCircle(sketch, "E63", {"center": v(72.07, 133.63) * mm, "radius": 2.54 * mm});
            skCircle(sketch, "E64", {"center": v(69.53, 129.23) * mm, "radius": 2.54 * mm});
            skCircle(sketch, "E65", {"center": v(79.7, 129.23) * mm, "radius": 2.54 * mm});
            skCircle(sketch, "E66.1.0", {"center": v(-78.42, 127.03) * mm, "radius": 2.54 * mm});
            skCircle(sketch, "E66.1.1", {"center": v(-75.88, 127.03) * mm, "radius": 2.54 * mm});
            skCircle(sketch, "E66.1.2", {"center": v(-75.88, 131.43) * mm, "radius": 2.54 * mm});
            skLineSegment(sketch, "E66.1.3", {"start": v(-73.34, 127.03) * mm, "end": v(-75.88, 127.03) * mm, "construction": true});
            skCircle(sketch, "E66.1.4", {"center": v(-79.7, 129.23) * mm, "radius": 2.54 * mm});
            skCircle(sketch, "E66.1.5", {"center": v(-74.61, 124.83) * mm, "radius": 2.54 * mm});
            skCircle(sketch, "E66.1.6", {"center": v(-78.42, 131.43) * mm, "radius": 2.54 * mm});
            skCircle(sketch, "E66.1.7", {"center": v(-70.8, 127.03) * mm, "radius": 2.54 * mm});
            skCircle(sketch, "E66.1.8", {"center": v(-77.15, 124.83) * mm, "radius": 2.54 * mm});
            skCircle(sketch, "E66.1.9", {"center": v(-73.34, 131.43) * mm, "radius": 2.54 * mm});
            skCircle(sketch, "E66.1.10", {"center": v(-70.8, 131.43) * mm, "radius": 2.54 * mm});
            skCircle(sketch, "E66.1.11", {"center": v(-77.15, 133.63) * mm, "radius": 2.54 * mm});
            skCircle(sketch, "E66.1.12", {"center": v(-69.53, 129.23) * mm, "radius": 2.54 * mm});
            skCircle(sketch, "E66.1.13", {"center": v(-72.07, 124.83) * mm, "radius": 2.54 * mm});
            skCircle(sketch, "E66.1.14", {"center": v(-73.34, 127.03) * mm, "radius": 2.54 * mm});
            skCircle(sketch, "E66.1.15", {"center": v(-72.07, 129.23) * mm, "radius": 2.54 * mm});
            skCircle(sketch, "E66.1.16", {"center": v(-74.61, 129.23) * mm, "radius": 2.54 * mm, "construction": true});
            skLineSegment(sketch, "E66.1.17", {"start": v(-73.34, 131.43) * mm, "end": v(-72.07, 129.23) * mm, "construction": true});
            skLineSegment(sketch, "E66.1.18", {"start": v(-75.88, 131.43) * mm, "end": v(-73.34, 131.43) * mm, "construction": true});
            skLineSegment(sketch, "E66.1.19", {"start": v(-77.15, 129.23) * mm, "end": v(-75.88, 131.43) * mm, "construction": true});
            skLineSegment(sketch, "E66.1.20", {"start": v(-75.88, 127.03) * mm, "end": v(-77.15, 129.23) * mm, "construction": true});
            skCircle(sketch, "E66.1.21", {"center": v(-74.61, 133.63) * mm, "radius": 2.54 * mm});
            skCircle(sketch, "E66.1.22", {"center": v(-72.07, 133.63) * mm, "radius": 2.54 * mm});
            skCircle(sketch, "E66.1.23", {"center": v(-77.15, 129.23) * mm, "radius": 2.54 * mm});
            skLineSegment(sketch, "E66.1.24", {"start": v(-72.07, 129.23) * mm, "end": v(-73.34, 127.03) * mm, "construction": true});
            skCircle(sketch, "E66.2.0", {"center": v(-149.22, -4.4) * mm, "radius": 2.54 * mm});
            skCircle(sketch, "E66.2.1", {"center": v(-147.95, -2.2) * mm, "radius": 2.54 * mm});
            skCircle(sketch, "E66.2.2", {"center": v(-151.76, 0) * mm, "radius": 2.54 * mm});
            skLineSegment(sketch, "E66.2.3", {"start": v(-146.69, 0) * mm, "end": v(-147.96, -2.2) * mm, "construction": true});
            skCircle(sketch, "E66.2.4", {"center": v(-151.77, -4.4) * mm, "radius": 2.54 * mm});
            skCircle(sketch, "E66.2.5", {"center": v(-145.41, -2.2) * mm, "radius": 2.54 * mm});
            skCircle(sketch, "E66.2.6", {"center": v(-153.04, -2.2) * mm, "radius": 2.54 * mm});
            skCircle(sketch, "E66.2.7", {"center": v(-145.41, 2.2) * mm, "radius": 2.54 * mm});
            skCircle(sketch, "E66.2.8", {"center": v(-146.68, -4.4) * mm, "radius": 2.54 * mm});
            skCircle(sketch, "E66.2.9", {"center": v(-150.5, 2.2) * mm, "radius": 2.54 * mm});
            skCircle(sketch, "E66.2.10", {"center": v(-149.22, 4.4) * mm, "radius": 2.54 * mm});
            skCircle(sketch, "E66.2.11", {"center": v(-154.3, 0) * mm, "radius": 2.54 * mm});
            skCircle(sketch, "E66.2.12", {"center": v(-146.68, 4.4) * mm, "radius": 2.54 * mm});
            skCircle(sketch, "E66.2.13", {"center": v(-144.15, 0) * mm, "radius": 2.54 * mm});
            skCircle(sketch, "E66.2.14", {"center": v(-146.69, 0) * mm, "radius": 2.54 * mm});
            skCircle(sketch, "E66.2.15", {"center": v(-147.96, 2.2) * mm, "radius": 2.54 * mm});
            skCircle(sketch, "E66.2.16", {"center": v(-149.22, 0) * mm, "radius": 2.54 * mm, "construction": true});
            skLineSegment(sketch, "E66.2.17", {"start": v(-150.5, 2.2) * mm, "end": v(-147.96, 2.2) * mm, "construction": true});
            skLineSegment(sketch, "E66.2.18", {"start": v(-151.76, 0) * mm, "end": v(-150.5, 2.2) * mm, "construction": true});
            skLineSegment(sketch, "E66.2.19", {"start": v(-150.5, -2.2) * mm, "end": v(-151.76, 0) * mm, "construction": true});
            skLineSegment(sketch, "E66.2.20", {"start": v(-147.95, -2.2) * mm, "end": v(-150.5, -2.2) * mm, "construction": true});
            skCircle(sketch, "E66.2.21", {"center": v(-153.03, 2.2) * mm, "radius": 2.54 * mm});
            skCircle(sketch, "E66.2.22", {"center": v(-151.76, 4.4) * mm, "radius": 2.54 * mm});
            skCircle(sketch, "E66.2.23", {"center": v(-150.5, -2.2) * mm, "radius": 2.54 * mm});
            skLineSegment(sketch, "E66.2.24", {"start": v(-147.96, 2.2) * mm, "end": v(-146.69, 0) * mm, "construction": true});
            skCircle(sketch, "E66.3.0", {"center": v(-70.8, -131.43) * mm, "radius": 2.54 * mm});
            skCircle(sketch, "E66.3.1", {"center": v(-72.07, -129.23) * mm, "radius": 2.54 * mm});
            skCircle(sketch, "E66.3.2", {"center": v(-75.88, -131.43) * mm, "radius": 2.54 * mm});
            skLineSegment(sketch, "E66.3.3", {"start": v(-73.34, -127.03) * mm, "end": v(-72.07, -129.23) * mm, "construction": true});
            skCircle(sketch, "E66.3.4", {"center": v(-72.07, -133.63) * mm, "radius": 2.54 * mm});
            skCircle(sketch, "E66.3.5", {"center": v(-70.8, -127.03) * mm, "radius": 2.54 * mm});
            skCircle(sketch, "E66.3.6", {"center": v(-74.61, -133.63) * mm, "radius": 2.54 * mm});
            skCircle(sketch, "E66.3.7", {"center": v(-74.61, -124.83) * mm, "radius": 2.54 * mm});
            skCircle(sketch, "E66.3.8", {"center": v(-69.53, -129.23) * mm, "radius": 2.54 * mm});
            skCircle(sketch, "E66.3.9", {"center": v(-77.15, -129.23) * mm, "radius": 2.54 * mm});
            skCircle(sketch, "E66.3.10", {"center": v(-78.42, -127.03) * mm, "radius": 2.54 * mm});
            skCircle(sketch, "E66.3.11", {"center": v(-77.15, -133.63) * mm, "radius": 2.54 * mm});
            skCircle(sketch, "E66.3.12", {"center": v(-77.15, -124.83) * mm, "radius": 2.54 * mm});
            skCircle(sketch, "E66.3.13", {"center": v(-72.07, -124.83) * mm, "radius": 2.54 * mm});
            skCircle(sketch, "E66.3.14", {"center": v(-73.34, -127.03) * mm, "radius": 2.54 * mm});
            skCircle(sketch, "E66.3.15", {"center": v(-75.88, -127.03) * mm, "radius": 2.54 * mm});
            skCircle(sketch, "E66.3.16", {"center": v(-74.61, -129.23) * mm, "radius": 2.54 * mm, "construction": true});
            skLineSegment(sketch, "E66.3.17", {"start": v(-77.15, -129.23) * mm, "end": v(-75.88, -127.03) * mm, "construction": true});
            skLineSegment(sketch, "E66.3.18", {"start": v(-75.88, -131.43) * mm, "end": v(-77.15, -129.23) * mm, "construction": true});
            skLineSegment(sketch, "E66.3.19", {"start": v(-73.34, -131.43) * mm, "end": v(-75.88, -131.43) * mm, "construction": true});
            skLineSegment(sketch, "E66.3.20", {"start": v(-72.07, -129.23) * mm, "end": v(-73.34, -131.43) * mm, "construction": true});
            skCircle(sketch, "E66.3.21", {"center": v(-78.42, -131.43) * mm, "radius": 2.54 * mm});
            skCircle(sketch, "E66.3.22", {"center": v(-79.7, -129.23) * mm, "radius": 2.54 * mm});
            skCircle(sketch, "E66.3.23", {"center": v(-73.34, -131.43) * mm, "radius": 2.54 * mm});
            skLineSegment(sketch, "E66.3.24", {"start": v(-75.88, -127.03) * mm, "end": v(-73.34, -127.03) * mm, "construction": true});
            skCircle(sketch, "E66.4.0", {"center": v(78.42, -127.03) * mm, "radius": 2.54 * mm});
            skCircle(sketch, "E66.4.1", {"center": v(75.88, -127.03) * mm, "radius": 2.54 * mm});
            skCircle(sketch, "E66.4.2", {"center": v(75.88, -131.43) * mm, "radius": 2.54 * mm});
            skLineSegment(sketch, "E66.4.3", {"start": v(73.34, -127.03) * mm, "end": v(75.88, -127.03) * mm, "construction": true});
            skCircle(sketch, "E66.4.4", {"center": v(79.7, -129.23) * mm, "radius": 2.54 * mm});
            skCircle(sketch, "E66.4.5", {"center": v(74.61, -124.83) * mm, "radius": 2.54 * mm});
            skCircle(sketch, "E66.4.6", {"center": v(78.42, -131.43) * mm, "radius": 2.54 * mm});
            skCircle(sketch, "E66.4.7", {"center": v(70.8, -127.03) * mm, "radius": 2.54 * mm});
            skCircle(sketch, "E66.4.8", {"center": v(77.15, -124.83) * mm, "radius": 2.54 * mm});
            skCircle(sketch, "E66.4.9", {"center": v(73.34, -131.43) * mm, "radius": 2.54 * mm});
            skCircle(sketch, "E66.4.10", {"center": v(70.8, -131.43) * mm, "radius": 2.54 * mm});
            skCircle(sketch, "E66.4.11", {"center": v(77.15, -133.63) * mm, "radius": 2.54 * mm});
            skCircle(sketch, "E66.4.12", {"center": v(69.53, -129.23) * mm, "radius": 2.54 * mm});
            skCircle(sketch, "E66.4.13", {"center": v(72.07, -124.83) * mm, "radius": 2.54 * mm});
            skCircle(sketch, "E66.4.14", {"center": v(73.34, -127.03) * mm, "radius": 2.54 * mm});
            skCircle(sketch, "E66.4.15", {"center": v(72.07, -129.23) * mm, "radius": 2.54 * mm});
            skCircle(sketch, "E66.4.16", {"center": v(74.61, -129.23) * mm, "radius": 2.54 * mm, "construction": true});
            skLineSegment(sketch, "E66.4.17", {"start": v(73.34, -131.43) * mm, "end": v(72.07, -129.23) * mm, "construction": true});
            skLineSegment(sketch, "E66.4.18", {"start": v(75.88, -131.43) * mm, "end": v(73.34, -131.43) * mm, "construction": true});
            skLineSegment(sketch, "E66.4.19", {"start": v(77.15, -129.23) * mm, "end": v(75.88, -131.43) * mm, "construction": true});
            skLineSegment(sketch, "E66.4.20", {"start": v(75.88, -127.03) * mm, "end": v(77.15, -129.23) * mm, "construction": true});
            skCircle(sketch, "E66.4.21", {"center": v(74.61, -133.63) * mm, "radius": 2.54 * mm});
            skCircle(sketch, "E66.4.22", {"center": v(72.07, -133.63) * mm, "radius": 2.54 * mm});
            skCircle(sketch, "E66.4.23", {"center": v(77.15, -129.23) * mm, "radius": 2.54 * mm});
            skLineSegment(sketch, "E66.4.24", {"start": v(72.07, -129.23) * mm, "end": v(73.34, -127.03) * mm, "construction": true});
            skCircle(sketch, "E66.5.0", {"center": v(149.22, 4.4) * mm, "radius": 2.54 * mm});
            skCircle(sketch, "E66.5.1", {"center": v(147.95, 2.2) * mm, "radius": 2.54 * mm});
            skCircle(sketch, "E66.5.2", {"center": v(151.76, 0) * mm, "radius": 2.54 * mm});
            skLineSegment(sketch, "E66.5.3", {"start": v(146.69, 0) * mm, "end": v(147.96, 2.2) * mm, "construction": true});
            skCircle(sketch, "E66.5.4", {"center": v(151.77, 4.4) * mm, "radius": 2.54 * mm});
            skCircle(sketch, "E66.5.5", {"center": v(145.41, 2.2) * mm, "radius": 2.54 * mm});
            skCircle(sketch, "E66.5.6", {"center": v(153.04, 2.2) * mm, "radius": 2.54 * mm});
            skCircle(sketch, "E66.5.7", {"center": v(145.41, -2.2) * mm, "radius": 2.54 * mm});
            skCircle(sketch, "E66.5.8", {"center": v(146.68, 4.4) * mm, "radius": 2.54 * mm});
            skCircle(sketch, "E66.5.9", {"center": v(150.5, -2.2) * mm, "radius": 2.54 * mm});
            skCircle(sketch, "E66.5.10", {"center": v(149.22, -4.4) * mm, "radius": 2.54 * mm});
            skCircle(sketch, "E66.5.11", {"center": v(154.3, 0) * mm, "radius": 2.54 * mm});
            skCircle(sketch, "E66.5.12", {"center": v(146.68, -4.4) * mm, "radius": 2.54 * mm});
            skCircle(sketch, "E66.5.13", {"center": v(144.15, 0) * mm, "radius": 2.54 * mm});
            skCircle(sketch, "E66.5.14", {"center": v(146.69, 0) * mm, "radius": 2.54 * mm});
            skCircle(sketch, "E66.5.15", {"center": v(147.96, -2.2) * mm, "radius": 2.54 * mm});
            skCircle(sketch, "E66.5.16", {"center": v(149.22, 0) * mm, "radius": 2.54 * mm, "construction": true});
            skLineSegment(sketch, "E66.5.17", {"start": v(150.5, -2.2) * mm, "end": v(147.96, -2.2) * mm, "construction": true});
            skLineSegment(sketch, "E66.5.18", {"start": v(151.76, 0) * mm, "end": v(150.5, -2.2) * mm, "construction": true});
            skLineSegment(sketch, "E66.5.19", {"start": v(150.5, 2.2) * mm, "end": v(151.76, 0) * mm, "construction": true});
            skLineSegment(sketch, "E66.5.20", {"start": v(147.95, 2.2) * mm, "end": v(150.5, 2.2) * mm, "construction": true});
            skCircle(sketch, "E66.5.21", {"center": v(153.03, -2.2) * mm, "radius": 2.54 * mm});
            skCircle(sketch, "E66.5.22", {"center": v(151.76, -4.4) * mm, "radius": 2.54 * mm});
            skCircle(sketch, "E66.5.23", {"center": v(150.5, 2.2) * mm, "radius": 2.54 * mm});
            skLineSegment(sketch, "E66.5.24", {"start": v(147.96, -2.2) * mm, "end": v(146.69, 0) * mm, "construction": true});
            skPoint(sketch, "E66.center", {"position": v(0, 0) * mm});
            skSolve(sketch);
        }
        {
            var Q0;
            Q0=makeQuery(id+"F2.imprint","IMPRINT",FACE,{"disambiguationData":[TD([[makeQuery(id+"F2.imprint","IMPRINT",EDGE,{"derivedFrom":makeQuery(id+"F0.imprint","IMPRINT",EDGE,{"derivedFrom":sQuery(id+"F0.wireOp",EDGE,"E0")})}),1.0]])]});
            var sketch = newSketch(context, id + "F4", { "sketchPlane" : qUnion([Q0])});
            skLineSegment(sketch, "E67.bottom", {"start": v(6.35, 152.4) * mm, "end": v(-6.35, 152.4) * mm});
            skLineSegment(sketch, "E67.top", {"start": v(6.35, -152.4) * mm, "end": v(-6.35, -152.4) * mm});
            skLineSegment(sketch, "E67.left", {"start": v(6.35, 152.4) * mm, "end": v(6.35, 2.63) * mm});
            skLineSegment(sketch, "E67.right", {"start": v(-6.35, 152.4) * mm, "end": v(-6.35, 2.63) * mm});
            skLineSegment(sketch, "E68", {"start": v(0, 0) * mm, "end": v(105.7, -105.7) * mm, "construction": true});
            skLineSegment(sketch, "E69.0", {"start": v(6.35, 2.63) * mm, "end": v(109.62, -100.64) * mm});
            skLineSegment(sketch, "E70.0", {"start": v(6.35, -15.33) * mm, "end": v(100.64, -109.62) * mm});
            skLineSegment(sketch, "E71", {"start": v(109.62, -100.64) * mm, "end": v(100.64, -109.62) * mm});
            skLineSegment(sketch, "E72", {"start": v(0, 0) * mm, "end": v(-104.92, -104.92) * mm, "construction": true});
            skLineSegment(sketch, "E73.0", {"start": v(-6.35, 2.63) * mm, "end": v(-6.35, 2.63) * mm});
            skLineSegment(sketch, "E74.0", {"start": v(-6.35, -15.33) * mm, "end": v(-100.64, -109.62) * mm});
            skLineSegment(sketch, "E75", {"start": v(-100.64, -109.62) * mm, "end": v(-109.62, -100.64) * mm});
            skLineSegment(sketch, "E76", {"start": v(6.35, -15.33) * mm, "end": v(6.35, -152.4) * mm});
            skLineSegment(sketch, "E77", {"start": v(6.35, 2.63) * mm, "end": v(6.35, -15.33) * mm, "construction": true});
            skLineSegment(sketch, "E78", {"start": v(-6.35, 2.63) * mm, "end": v(-109.62, -100.64) * mm});
            skLineSegment(sketch, "E79", {"start": v(-6.35, -15.33) * mm, "end": v(-6.35, -152.4) * mm});
            skLineSegment(sketch, "E80", {"start": v(-6.35, 2.63) * mm, "end": v(-6.35, -15.33) * mm, "construction": true});
            skSolve(sketch);
        }
        {
            var Q0;
            Q0=qCreatedBy(makeId("Front.planeOp"),FACE);
            var sketch = newSketch(context, id + "F5", { "sketchPlane" : qUnion([Q0])});
            skLineSegment(sketch, "E81", {"start": v(0, 0) * mm, "end": v(38.62, 144.14) * mm, "construction": true});
            skSolve(sketch);
        }
        {
            var Q0;
            Q0=sQuery(id+"F5.wireOp",VERTEX,"E81.end");
            var Q1;
            Q1=makeQuery(id+"F1.opExtrude","SWEPT_BODY",BODY,{"disambiguationData":[OSD([sQuery(id+"F0.wireOp",EDGE,"E0"),sQuery(id+"F0.wireOp",EDGE,"E1"),sQuery(id+"F0.wireOp",EDGE,"E3")])]});
            hole(context, id + "F6", {"style" : HoleStyle.SIMPLE, "endStyle" : HoleEndStyle.BLIND, "oppositeDirection" : true, "holeDiameter" : 6.35 * mm, "majorDiameter" : 6.35 * mm, "holeDepth" : 50.8 * mm, "isTappedThrough" : true, "tappedDepth" : 12.7 * mm, "tapClearance" : 3, "locations" : qUnion([Q0]), "scope" : qUnion([Q1])});
        }
    });
